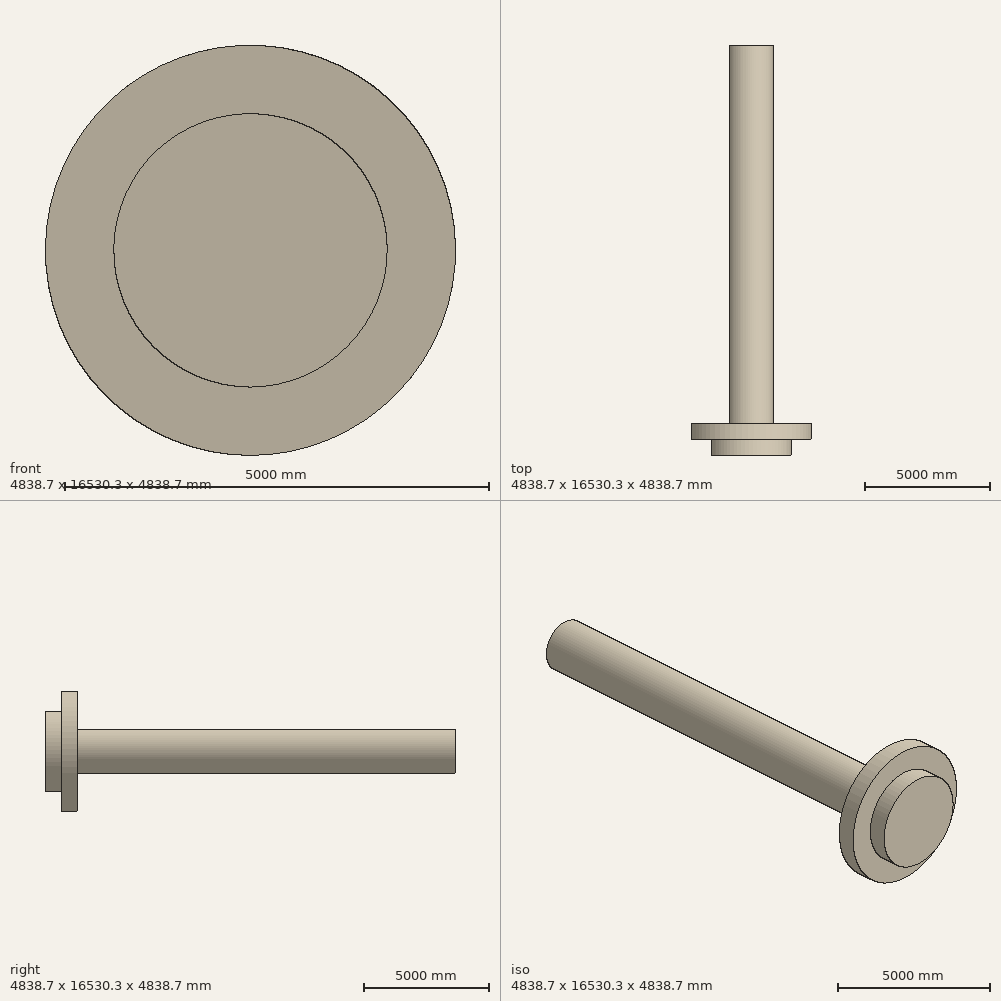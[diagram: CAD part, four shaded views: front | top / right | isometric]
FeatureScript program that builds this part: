
annotation { "Feature Type Name" : "Feature", "Feature Type Description" : "" }
export const myFeature = defineFeature(function(context is Context, id is Id, definition is map)
    precondition{}
    {
        {
            var Q0;
            Q0=qCreatedBy(makeId("Right.planeOp"),FACE);
            var sketch = newSketch(context, id + "F0", { "sketchPlane" : qUnion([Q0])});
            skLineSegment(sketch, "E0.bottom", {"start": v(0, 0) * mm, "end": v(645.16, 0) * mm});
            skLineSegment(sketch, "E0.top", {"start": v(0, 2419.35) * mm, "end": v(645.16, 2419.35) * mm});
            skLineSegment(sketch, "E0.left", {"start": v(0, 0) * mm, "end": v(0, 2419.35) * mm});
            skLineSegment(sketch, "E0.right", {"start": v(645.16, 0) * mm, "end": v(645.16, 2419.35) * mm});
            skLineSegment(sketch, "E1.bottom", {"start": v(645.16, 0) * mm, "end": v(15885.16, 0) * mm});
            skLineSegment(sketch, "E1.top", {"start": v(645.16, 889) * mm, "end": v(15885.16, 889) * mm});
            skLineSegment(sketch, "E1.left", {"start": v(645.16, 0) * mm, "end": v(645.16, 889) * mm});
            skLineSegment(sketch, "E1.right", {"start": v(15885.16, 0) * mm, "end": v(15885.16, 889) * mm});
            skLineSegment(sketch, "E2.bottom", {"start": v(0, 1612.9) * mm, "end": v(-645.16, 1612.9) * mm});
            skLineSegment(sketch, "E2.top", {"start": v(0, 0) * mm, "end": v(-645.16, 0) * mm});
            skLineSegment(sketch, "E2.left", {"start": v(0, 1612.9) * mm, "end": v(0, 0) * mm});
            skLineSegment(sketch, "E2.right", {"start": v(-645.16, 1612.9) * mm, "end": v(-645.16, 0) * mm});
            skSolve(sketch);
        }
        {
            var Q0;
            Q0 = qSketchRegion(id + "F0", true);
            var Q1;
            Q1=sQuery(id+"F0.wireOp",EDGE,"E1.bottom");
            revolve(context, id + "F1", {"entities" : qUnion([Q0]), "axis" : qUnion([Q1]), "revolveType" : RevolveType.FULL});
        }
    });
